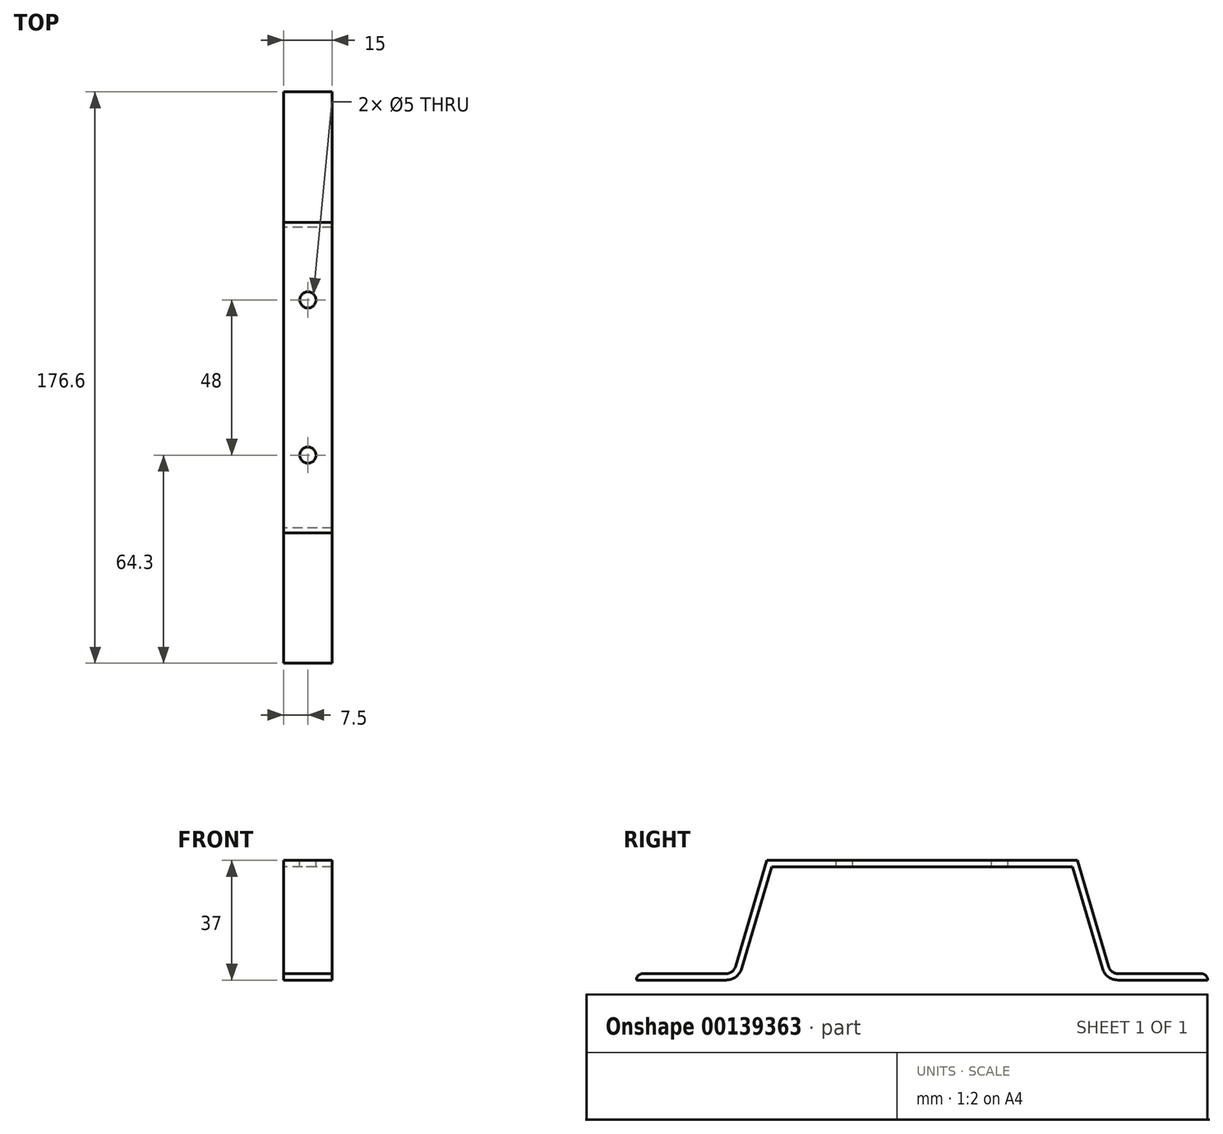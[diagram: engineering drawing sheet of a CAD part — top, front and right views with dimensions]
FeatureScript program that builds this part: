
annotation { "Feature Type Name" : "Feature", "Feature Type Description" : "" }
export const myFeature = defineFeature(function(context is Context, id is Id, definition is map)
    precondition{}
    {
        {
            var Q0;
            Q0=qCreatedBy(makeId("Right.planeOp"),FACE);
            var sketch = newSketch(context, id + "F0", { "sketchPlane" : qUnion([Q0])});
            skLineSegment(sketch, "E0", {"start": v(-88.3, 0) * mm, "end": v(-58.3, 0) * mm});
            skLineSegment(sketch, "E1", {"start": v(-58.3, 0) * mm, "end": v(-48, 35) * mm});
            skLineSegment(sketch, "E2", {"start": v(-48, 35) * mm, "end": v(0, 35) * mm});
            skLineSegment(sketch, "E3.0", {"start": v(-46.5, 33) * mm, "end": v(0, 33) * mm});
            skLineSegment(sketch, "E3.1", {"start": v(-56.8, -2) * mm, "end": v(-46.5, 33) * mm});
            skLineSegment(sketch, "E3.2", {"start": v(-88.3, -2) * mm, "end": v(-56.8, -2) * mm});
            skLineSegment(sketch, "E4", {"start": v(-88.3, 0) * mm, "end": v(-88.3, -2) * mm});
            skLineSegment(sketch, "E5.MirrorCS", {"start": v(48, 35) * mm, "end": v(0, 35) * mm});
            skLineSegment(sketch, "E6.MirrorCS", {"start": v(46.5, 33) * mm, "end": v(0, 33) * mm});
            skLineSegment(sketch, "E7.MirrorCS", {"start": v(56.8, -2) * mm, "end": v(46.5, 33) * mm});
            skLineSegment(sketch, "E8.MirrorCS", {"start": v(58.3, 0) * mm, "end": v(48, 35) * mm});
            skLineSegment(sketch, "E9.MirrorCS", {"start": v(88.3, -2) * mm, "end": v(56.8, -2) * mm});
            skLineSegment(sketch, "E10.MirrorCS", {"start": v(88.3, 0) * mm, "end": v(58.3, 0) * mm});
            skLineSegment(sketch, "E11.MirrorCS", {"start": v(88.3, 0) * mm, "end": v(88.3, -2) * mm});
            skSolve(sketch);
        }
        {
            var Q0;
            Q0 = qSketchRegion(id + "F0", true);
            extrude(context, id + "F1", {"entities" : qUnion([Q0]), "endBound" : BoundingType.SYMMETRIC, "depth" : 15 * mm});
        }
        {
            var Q0;
            Q0=makeQuery(id+"F1.opExtrude","SWEPT_FACE",FACE,{"disambiguationData":[OSD([sQuery(id+"F0.wireOp",EDGE,"E2"),sQuery(id+"F0.wireOp",EDGE,"E5.MirrorCS")])]});
            var sketch = newSketch(context, id + "F2", { "sketchPlane" : qUnion([Q0])});
            skCircle(sketch, "E12", {"center": v(0, -24) * mm, "radius": 2.5 * mm});
            skCircle(sketch, "E13.MirrorC", {"center": v(0, 24) * mm, "radius": 2.5 * mm});
            skSolve(sketch);
        }
        {
            var Q0;
            Q0 = qSketchRegion(id + "F2", true);
            extrude(context, id + "F3", {"entities" : qUnion([Q0]), "operationType" : NewBodyOperationType.REMOVE, "oppositeDirection" : true, "depth" : 2 * mm});
        }
        {
            var Q0;
            Q0=makeQuery(id+"F1.opExtrude","SWEPT_EDGE",EDGE,{"disambiguationData":[OSD([sQuery(id+"F0.wireOp",EDGE,"E3.1"),sQuery(id+"F0.wireOp",EDGE,"E3.2")])]});
            fillet(context, id + "F4", {"entities" : qUnion([Q0]), "radius" : 5 * mm, "tangentPropagation" : true, "allowEdgeOverflow" : false});
        }
        {
            var Q0;
            Q0=makeQuery(id+"F1.opExtrude","SWEPT_EDGE",EDGE,{"disambiguationData":[OSD([sQuery(id+"F0.wireOp",EDGE,"E0"),sQuery(id+"F0.wireOp",EDGE,"E1")])]});
            fillet(context, id + "F5", {"entities" : qUnion([Q0]), "radius" : 3 * mm, "tangentPropagation" : true, "allowEdgeOverflow" : false});
        }
        {
            var Q0;
            Q0=makeQuery(id+"F1.opExtrude","SWEPT_EDGE",EDGE,{"disambiguationData":[OSD([sQuery(id+"F0.wireOp",EDGE,"E8.MirrorCS"),sQuery(id+"F0.wireOp",EDGE,"E10.MirrorCS")])]});
            fillet(context, id + "F6", {"entities" : qUnion([Q0]), "radius" : 3 * mm, "tangentPropagation" : true, "allowEdgeOverflow" : false});
        }
        {
            var Q0;
            Q0=makeQuery(id+"F1.opExtrude","SWEPT_EDGE",EDGE,{"disambiguationData":[OSD([sQuery(id+"F0.wireOp",EDGE,"E7.MirrorCS"),sQuery(id+"F0.wireOp",EDGE,"E9.MirrorCS")])]});
            fillet(context, id + "F7", {"entities" : qUnion([Q0]), "radius" : 5 * mm, "tangentPropagation" : true, "allowEdgeOverflow" : false});
        }
        {
            var Q0;
            Q0=makeQuery(id+"F1.opExtrude","SWEPT_EDGE",EDGE,{"disambiguationData":[OSD([sQuery(id+"F0.wireOp",EDGE,"E0"),sQuery(id+"F0.wireOp",EDGE,"E4")])]});
            var Q1;
            Q1=makeQuery(id+"F1.opExtrude","SWEPT_EDGE",EDGE,{"disambiguationData":[OSD([sQuery(id+"F0.wireOp",EDGE,"E10.MirrorCS"),sQuery(id+"F0.wireOp",EDGE,"E11.MirrorCS")])]});
            fillet(context, id + "F8", {"entities" : qUnion([Q0, Q1]), "radius" : 2 * mm, "tangentPropagation" : true, "allowEdgeOverflow" : false});
        }
    });
